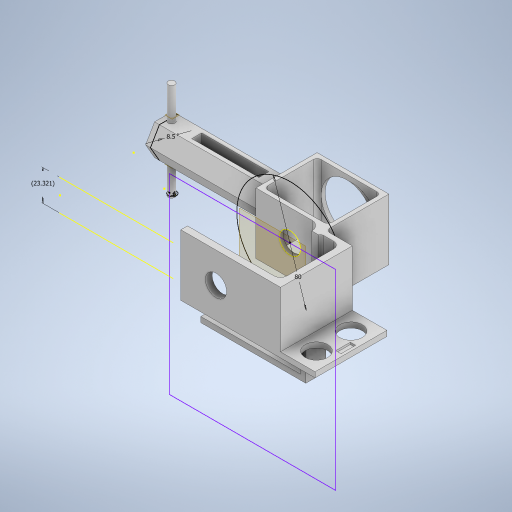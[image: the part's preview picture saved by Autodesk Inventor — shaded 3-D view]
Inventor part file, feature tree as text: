
AUTODESK INVENTOR PART (.ipt)
format: ipt  version: 2024 (Build 280153000, 153)  size: 859,136 bytes
history: native  units: in
note: dims shown in document units (in); Inventor stores cm internally (conversion verified against a paired STEP export)
features: sketch x55, extrude x49, fillet x12, plane x3
ambient origin geometry x8: Origin, YZ Plane, XZ Plane, XY Plane, X Axis, Y Axis, Z Axis, Center Point
bodies: Solid1 (feature_tree)
feature tree (119):
  extrude  "Extrusion1"  Depth=0.0984in
  extrude  "Extrusion2"  Depth=0.3937in TaperAngle=0.0deg
  extrude  "Extrusion3"  Depth=0.3937in TaperAngle=0.0deg
  extrude  "Extrusion4"  Depth=0.1969in
  fillet  "Fillet1"  Radius=2.7559in
  fillet  "Fillet2"  Radius=0.1969in
  extrude  "Extrusion5"  Depth=0.0984in
  extrude  "Extrusion6"  Depth=1.811in
  extrude  "Extrusion7"  Depth=1.811in TaperAngle=0.0deg
  extrude  "Extrusion8"  Depth=0.1181in
  extrude  "Extrusion9"  Depth=0.1181in TaperAngle=0.0deg
  fillet  "Fillet3"  Radius=0.6693in
  fillet  "Fillet4"  Radius=0.1181in
  plane  "Work Plane1"
  extrude  "Extrusion15"  Depth=0.6299in
  extrude  "Extrusion18"  Depth=0.1181in
  extrude  "Extrusion19"  Depth=0.3937in
  extrude  "Extrusion20"  Depth=0.2756in
  extrude  "Extrusion21"  Depth=0.1969in TaperAngle=0.0deg
  extrude  "Extrusion26"  Depth=0.1575in
  fillet  "Fillet9"  Radius=0.7874in
  fillet  "Fillet10"  Radius=0.1969in
  fillet  "Fillet11"  Radius=1.9685in
  fillet  "Fillet12"  Radius=0.1969in
  fillet  "Fillet13"  Radius=2.7559in
  fillet  "Fillet15"  Radius=11.811in
  plane  "Work Plane2"
  extrude  "Extrusion27"  Depth=0.1181in
  plane  "Work Plane3"
  extrude  "Extrusion28"  Depth=0.1969in
  extrude  "Extrusion29"  Depth=0.1575in
  extrude  "Extrusion30"  Depth=0.315in
  sketch  "Sketch35"  dims[d121=0.1181in d122=0.0in d123=-0.748in]
  extrude  "Extrusion31"  [1 undecoded]
  extrude  "Extrusion32"  Depth=0.1575in
  extrude  "Extrusion33"  Depth=3.937in
  extrude  "Extrusion34"  Depth=0.1575in
  extrude  "Extrusion35"  Depth=0.1575in
  extrude  "Extrusion36"  Depth=0.6299in TaperAngle=0.0deg
  extrude  "Extrusion37"  Depth=0.1181in TaperAngle=0.0deg
  extrude  "Extrusion38"  Depth=0.4724in
  extrude  "Extrusion39"  Depth=3.937in TaperAngle=0.0deg
  extrude  "Extrusion40"  Depth=3.937in TaperAngle=0.0deg
  sketch  "Sketch46"  dims[d152=3.1496in d153=0.0in d154=0.4331in]
  extrude  "Extrusion41"  Depth=0.1181in
  extrude  "Extrusion42"  Depth=0.4331in
  extrude  "Extrusion43"  Depth=0.3937in
  extrude  "Extrusion44"  Depth=0.2362in
  extrude  "Extrusion45"  Depth=0.9843in TaperAngle=0.0deg
  extrude  "Extrusion46"  Depth=0.1969in
  extrude  "Extrusion47"  Depth=0.1181in
  fillet  "Fillet16"  Radius=0.1181in
  fillet  "Fillet17"  Radius=0.1181in
  extrude  "Extrusion48"  Depth=0.1181in TaperAngle=0.0deg
  extrude  "Extrusion49"  Depth=0.1969in TaperAngle=0.0deg
  sketch  "Sketch56"  dims[d182=0.6299in d183=39.3701in d184=0.0in]
  extrude  "Extrusion50"  Depth=0.4331in TaperAngle=0.0deg
  extrude  "Extrusion51"  Depth=0.6299in TaperAngle=0.0deg
  extrude  "Extrusion52"  Depth=0.1181in TaperAngle=0.0deg
  extrude  "Extrusion53"  Depth=0.2756in
  sketch  "Sketch61"  dims[d196=1.0236in d197=0.0in d198=0.5118in]
  extrude  "Extrusion54"  Depth=0.1181in TaperAngle=0.0deg
  extrude  "Extrusion55"  Depth=0.1575in
  sketch  "Sketch65"  dims[d204=0.0591in d205=0.0in d206=0.0787in]
  extrude  "Extrusion58"  Depth=0.5118in
  extrude  "Extrusion59"  Depth=0.6693in TaperAngle=0.0deg
  sketch  "Sketch69"  dims[d211=3.1496in]
  sketch  "Sketch72"  dims[d212=0.1575in]
  extrude  "Extrusion62"  Depth=0.4331in
  extrude  "Extrusion63"  Depth=0.0591in
  extrude  "Extrusion64"  Depth=0.5906in
  sketch  "Sketch1"  dims[d0=0.3937in d1=0.0984in]
  sketch  "Sketch2"  dims[d2=0.3937in d3=0.0in d4=0.0787in d5=0.0in]
  sketch  "Sketch3"  dims[d6=0.3937in d7=0.0787in d8=0.0in]
  sketch  "Sketch4"  dims[d9=0.2362in d10=0.1969in d11=2.7559in d12=0.0in d13=0.1969in]
  sketch  "Sketch5"  dims[d14=0.1575in d15=0.0984in]
  sketch  "Sketch6"  dims[d16=3.1496in d17=0.0in d18=1.811in]
  sketch  "Sketch8"  dims[d19=1.811in d20=2.126in d21=0.0in]
  sketch  "Sketch9"  dims[d22=0.1181in d23=0.1181in]
  sketch  "Sketch10"  dims[d24=0.1181in d25=1.7717in d26=0.0in d27=0.6693in d28=0.1181in d29=0.0in]
  sketch  "Sketch19"  dims[d30=0.9843in d31=0.6299in]
  sketch  "Sketch22"  dims[d32=1.378in d33=0.0in d34=0.1181in]
  sketch  "Sketch23"  dims[d35=0.0787in d36=0.3937in]
  sketch  "Sketch24"  dims[d72=0.3937in d73=0.0in d80=0.2756in]
  sketch  "Sketch25"  dims[d81=1.378in d82=0.1969in d83=0.0in]
  sketch  "Sketch30"  dims[d84=0.1378in d85=0.1575in d86=0.7874in d87=0.0in d88=0.1969in d89=1.9685in d90=0.0in d91=0.1969in d92=2.7559in d93=0.0in d110=11.811in d111=0.0in]
  sketch  "Sketch31"  dims[d112=0.1181in d113=0.1181in]
  sketch  "Sketch32"  dims[d114=0.2677in d115=0.1969in]
  sketch  "Sketch33"  dims[d116=0.1969in d118=0.1575in]
  sketch  "Sketch34"  dims[d119=-0.748in d120=0.315in]
  sketch  "Sketch36"  dims[d124=0.1181in d125=0.0in d126=0.1575in]
  sketch  "Sketch37"  dims[d127=3.937in d128=0.0in d129=0.7087in]
  sketch  "Sketch38"  dims[d130=0.1181in d131=0.0in d132=0.1575in]
  sketch  "Sketch39"  dims[d133=0.2362in d134=0.1575in]
  sketch  "Sketch40"  dims[d135=0.2362in d136=0.6299in d137=0.0in]
  sketch  "Sketch41"  dims[d138=0.7087in d139=0.1181in d140=0.0in]
  sketch  "Sketch42"  dims[d141=3.5827in d142=0.4724in]
  sketch  "Sketch43"  dims[d143=3.1102in d144=3.937in d145=0.0in]
  sketch  "Sketch44"  dims[d146=3.937in d147=0.0in d148=3.937in d149=0.0in]
  sketch  "Sketch45"  dims[d150=0.3937in d151=0.1181in]
  sketch  "Sketch47"  dims[d155=0.0984in d156=0.0in d157=0.3937in]
  sketch  "Sketch49"  dims[d158=0.3937in d159=0.0in d160=0.2362in]
  sketch  "Sketch50"  dims[d161=0.1969in d162=0.9843in d163=0.0in]
  sketch  "Sketch51"  dims[d164=0.2362in d165=0.1969in]
  sketch  "Sketch52"  dims[d166=0.9843in d167=0.0in d168=1.5354in d169=0.1181in d170=0.1181in]
  sketch  "Sketch53"  dims[d171=2.126in d172=0.0in d173=0.1181in d174=0.0in]
  sketch  "Sketch54"  dims[d175=0.1181in d176=0.0in d177=0.1969in d178=0.0in]
  sketch  "Sketch55"  dims[d179=0.1969in d180=0.4331in d181=0.0in]
  sketch  "Sketch57"  dims[d185=1.5354in d186=0.1181in d187=0.0in]
  sketch  "Sketch58"  dims[d188=0.1181in d189=0.2756in]
  sketch  "Sketch59"  dims[d190=0.1969in d191=0.0in d192=0.1181in d193=0.0in]
  sketch  "Sketch60"  dims[d194=0.9181in d195=0.1575in]
  sketch  "Sketch62"  dims[d199=0.6693in d200=1.0236in d201=0.0in]
  sketch  "Sketch63"  dims[d202=0.1575in d203=0.4331in]
  sketch  "Sketch67"  dims[d207=0.1575in d208=0.5906in]
  sketch  "Sketch68"  dims[d209=1.063in d210=0.0in]
  sketch  "Sketch73"  dims[d213=2.9528in d214=0.0in]
  sketch  "Sketch74"  dims[d215=0.1575in d216=0.0in]
  sketch  "Sketch75"  dims[d228=0.4094in d229=0.5906in d230=0.0in d231=0.8661in d232=0.1378in d233=0.0in d234=0.3346in d240=0.3346in d241=2.9528in d242=0.0in d243=0.3937in d244=0.1181in d245=0.3937in d247=0.1181in d248=0.2939in d249=2.9528in d250=0.0in d251=0.874in d252=0.6299in d253=0.1299in d254=1.5748in d256=360.0deg d258=0.1969in d259=0.0in d37=0.0in d38=0.0in d39=0.0in d74=0.0197in d75=0.0344in d238=0.0197in d239=0.0344in]
note: 1 required parameter value undecoded (feature->parameter linkage not recoverable at this tier; creation-order binding heuristic only, values carry confidence <= 0.55)
